# Revit family: PRD_FrankeWS_WlHngWshBsns_ANIMASingleWashbasin_ANMX462
name_source: partatom
category: Plumbing Fixtures
revit_build: Autodesk Revit 2018 (Build: 20190510_1515(x64)
units: mm (PartAtom-declared; Revit-internal decimal feet)

## family parameters
Cut with Voids When Loaded = Yes
Host = Face
OmniClass Number = 23.45.05.14.14.27
OmniClass Title = Service Sinks
Part Type = Normal
Room Calculation Point = No
Round Connector Dimension = Use Diameter
Shared = Yes

## types (1)
- ANMX462
    AssetType = Fixed
    BIMObjectName = PRD_AR_WallHungWashbasins_ANIMASingleWashbasin_ANMX462
    BowlDepth = 360.00 mm
    BowlFinish = Satin finish
    BowlHeight = 140.00 mm
    BowlPosition = Center
    BowlShape = Circle with straight sides
    BowlWidth = 420.00 mm
    Category = Pr_40_20_96_96, Wall-hung washbasins
    Default Elevation = 925 mm  [stored 3.03478 ft]
    Description = Single wash basin for wall-mounting, made of stainless steel, surface satin finished, material thickness 1.2 mm. Seamless wash basin in one piece with rounded edges, without tap landing, strainer waste valve, DN 40/50 siphon included, without overflow. Mounting from the front, fixing material included. Wash basin suitable for areas exposed to vandalism and wheelchair users.
    DiameterNominal = 50  [stored 0.164042 ft]
    DrainSize = 50 mm  [stored 0.164042 ft]
    DurationUnit = year
    Features = stainless steel, surface satin finished, material thickness 1.2 mm
    Finish = Satin finish
    Flow = 0.0 L/s
    GrossWeight = 8.36 kg
    IfcExportAs = IfcSanitaryTerminalType
    IfcExportType = WASHHANDBASIN
    IntegralAccessories = fixing material included
    Manufacturer = KWC Group AG
    ManufacturerName = KWC Group AG
    ManufacturerURL = www.kwc.com
    Material = stainless steel
    MaterialCode = 1.4301 Chrome Nickel steel V2A
    MaterialThickness = 1.20 mm
    Model = ANMX462
    ModelNumber = 2000102712
    ModelReference = ANMX462
    Mounting = WallHung
    MountingOffset = 0 mm  [stored 0 ft]
    NBSDescription = Wall hung wash basins
    NBSReference = 45-35-70/369
    Name = ANIMA Single washbasin ANMX462
    NetWeight = 7.94 kg
    NominalDepth = 410 mm  [stored 1.34514 ft]
    NominalHeight = 170 mm  [stored 0.557743 ft]
    NominalWidth = 460 mm  [stored 1.50919 ft]
    NumberOfBowls = 1
    NumberOfTapHoles = 0
    Overflow = No
    ProductCode = 203.0544.436
    ProductInformation = https://pim.kwc.com
    RearUpstand = No
    SinkMaterial = PRD_AR_StainlessSteel_SatinFinished
    SiphonDiameter = DN 50
    SiphonIncluded = Yes
    Size = 460 x 170 x 410 mm (W x H x D)
    Spillway = No
    Splashback = No
    TailorMade = No
    TapLedge = No
    TypeOfBasin = Wash basin
    TypeOfMounting = Wall mounting
    TypeOfWasteKit = Welded perforated waste (non removable)
    URL = www.kwc.com
    Uniclass2015Code = Pr_40_20_96_96
    Uniclass2015Title = Wall-hung washbasins
    Uniclass2015Version = Products v1.23
    Version = 1
    WarrantyDurationUnit = year
    WashHandBasinType = HandRinse
    WasteHolePosition = Center back
    WasteHoleProjection = 135.00 mm
    WasteKitIncluded = Yes
    WasteSize = DN 32

note: [stored X ft] marks values corroborated as IEEE doubles in the binary element streams (Revit-internal decimal feet)

## geometry (parser evidence)
native form markers: Sweep x5
no freeform markers — native parametric forms only
